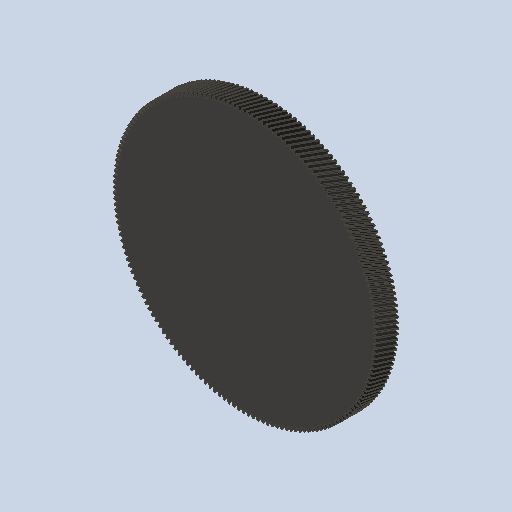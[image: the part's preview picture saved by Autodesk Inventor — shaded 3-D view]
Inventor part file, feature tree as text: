
AUTODESK INVENTOR PART (.ipt)
format: ipt  version: 2023 (Build 270158000, 158)  size: 1,938,432 bytes
history: native  units: mm (DEFAULTED — no unit token found)
features: plane x3, other x3, sketch x2, extrude x1
ambient origin geometry x8: Origin, YZ Plane, XZ Plane, XY Plane, X Axis, Y Axis, Z Axis, Center Point
bodies: Solid1 (feature_tree)
feature tree (9):
  extrude  "Extrusion1"  Depth=15.0mm TaperAngle=0.0deg
  plane  "Work Plane2"
  plane  "Work Plane8"
  plane  "Work Plane9"
  other  "Spur Gear"
  sketch  "Sketch1"  dims[d0=182.852267mm d1=15.0mm d2=0.0mm]
  sketch  "Sketch2"  dims[d3=180.910221mm d4=10.0mm d5=0.0mm d16=101.6mm d17=0.0mm d34=0.1848mm d39=0.0mm d41=0.0mm d43=101.6mm d46=101.6mm d47=0.0mm d48=0.0mm]
  other  "Srf1"
  other  "Pitch Diameter"
